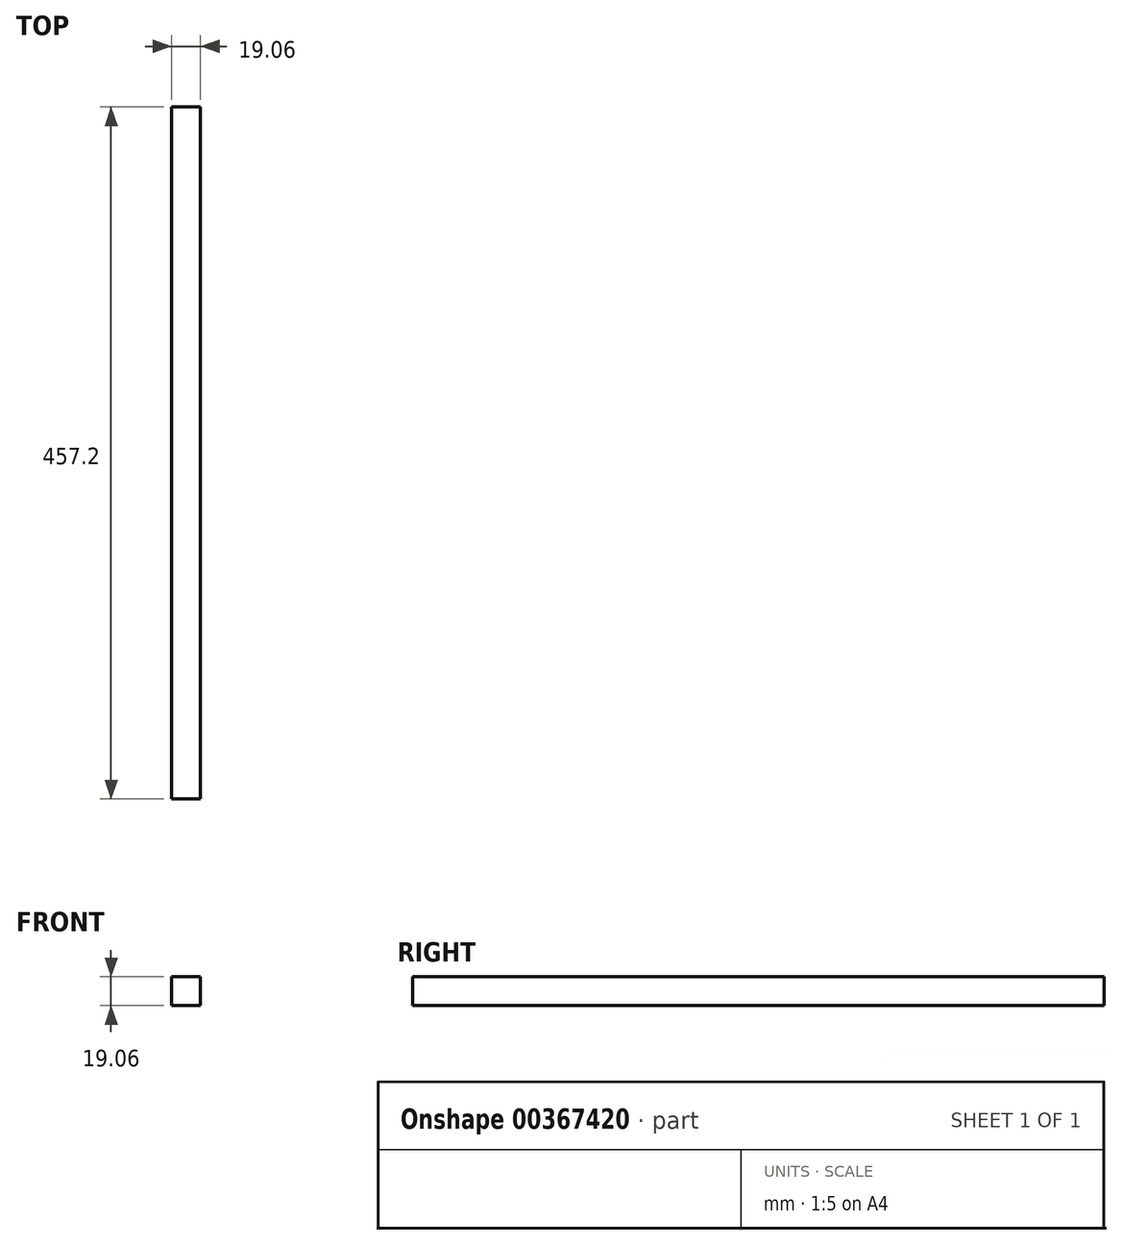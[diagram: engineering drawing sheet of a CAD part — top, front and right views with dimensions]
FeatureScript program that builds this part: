
annotation { "Feature Type Name" : "Feature", "Feature Type Description" : "" }
export const myFeature = defineFeature(function(context is Context, id is Id, definition is map)
    precondition{}
    {
        {
            var Q0;
            Q0=qCreatedBy(makeId("Front.planeOp"),FACE);
            var sketch = newSketch(context, id + "F0", { "sketchPlane" : qUnion([Q0])});
            skLineSegment(sketch, "E0.bottom", {"start": v(9.52, 9.53) * mm, "end": v(-9.53, 9.53) * mm});
            skLineSegment(sketch, "E0.top", {"start": v(9.53, -9.53) * mm, "end": v(-9.52, -9.53) * mm});
            skLineSegment(sketch, "E0.left", {"start": v(9.52, 9.53) * mm, "end": v(9.53, -9.53) * mm});
            skLineSegment(sketch, "E0.right", {"start": v(-9.53, 9.53) * mm, "end": v(-9.52, -9.53) * mm});
            skPoint(sketch, "E0.middle", {"position": v(0, 0) * mm});
            skSolve(sketch);
        }
        {
            var Q0;
            Q0 = qSketchRegion(id + "F0", true);
            extrude(context, id + "F1", {"entities" : qUnion([Q0]), "depth" : 457.2 * mm});
        }
    });
